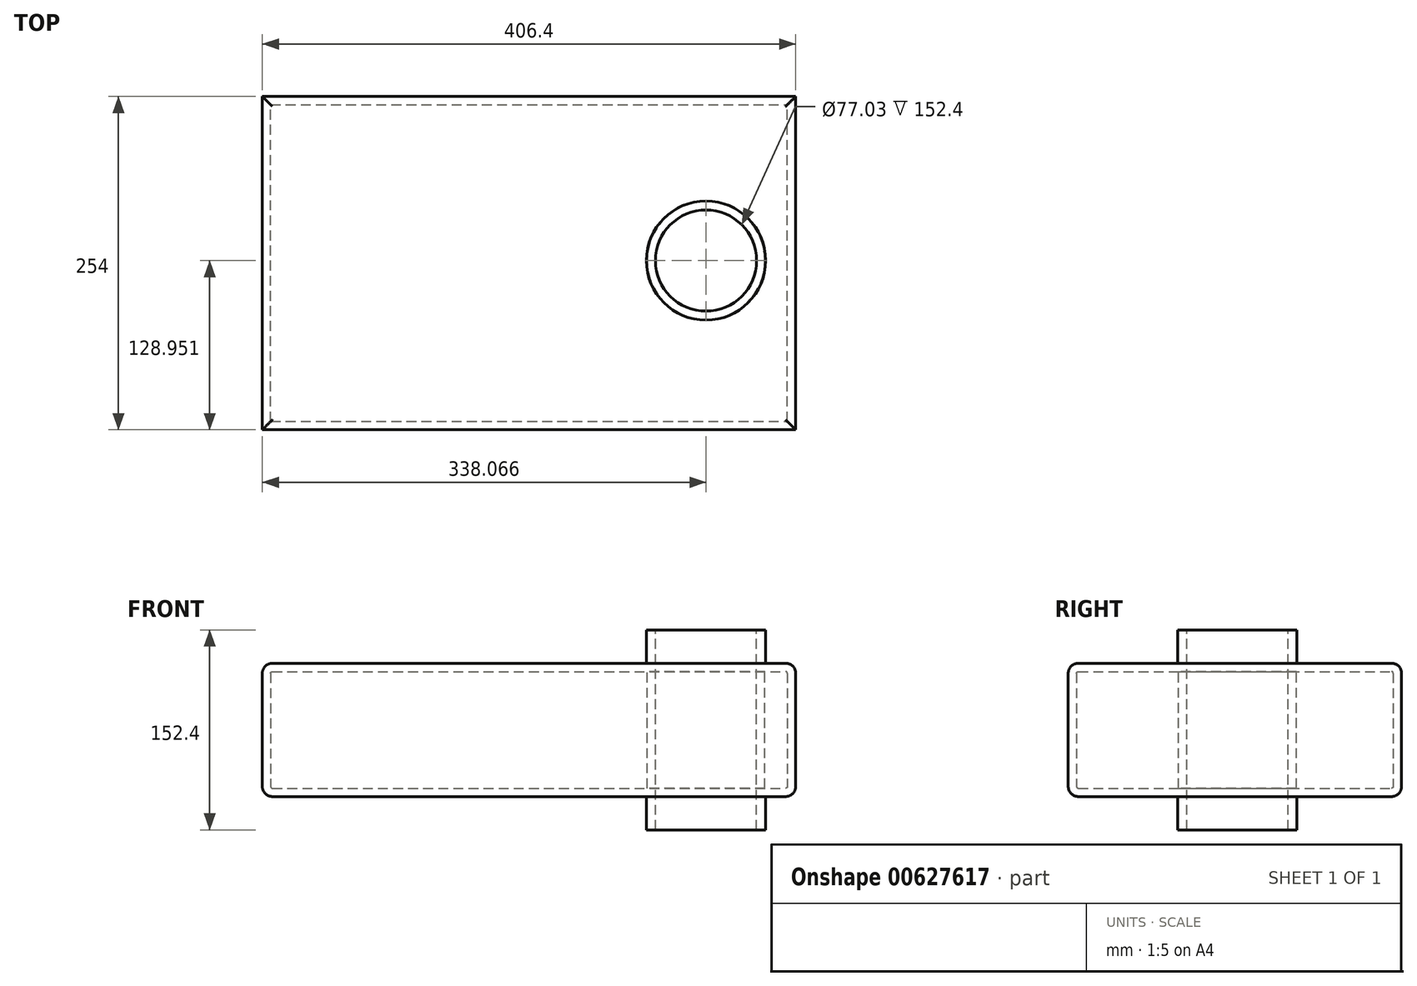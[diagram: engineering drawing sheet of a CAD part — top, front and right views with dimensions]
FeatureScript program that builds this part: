
annotation { "Feature Type Name" : "Feature", "Feature Type Description" : "" }
export const myFeature = defineFeature(function(context is Context, id is Id, definition is map)
    precondition{}
    {
        {
            var Q0;
            Q0=qCreatedBy(makeId("Top.planeOp"),FACE);
            var sketch = newSketch(context, id + "F0", { "sketchPlane" : qUnion([Q0])});
            skLineSegment(sketch, "E0.bottom", {"start": v(-406.4, 0) * mm, "end": v(0, 0) * mm});
            skLineSegment(sketch, "E0.top", {"start": v(-406.4, 254) * mm, "end": v(0, 254) * mm});
            skLineSegment(sketch, "E0.left", {"start": v(-406.4, 0) * mm, "end": v(-406.4, 254) * mm});
            skLineSegment(sketch, "E0.right", {"start": v(0, 0) * mm, "end": v(0, 254) * mm});
            skSolve(sketch);
        }
        {
            var Q0;
            Q0 = qSketchRegion(id + "F0", true);
            extrude(context, id + "F1", {"entities" : qUnion([Q0]), "depth" : 50.8 * mm, "offsetDistance" : 25.4 * mm});
        }
        {
            var Q0;
            Q0=makeQuery(id+"F1.opExtrude","CAP_EDGE",EDGE,{"disambiguationData":[OSD([sQuery(id+"F0.wireOp",EDGE,"E0.left")])],"isStart":false});
            var Q1;
            Q1=makeQuery(id+"F1.opExtrude","CAP_EDGE",EDGE,{"disambiguationData":[OSD([sQuery(id+"F0.wireOp",EDGE,"E0.bottom")])],"isStart":false});
            var Q2;
            Q2=makeQuery(id+"F1.opExtrude","CAP_EDGE",EDGE,{"disambiguationData":[OSD([sQuery(id+"F0.wireOp",EDGE,"E0.right")])],"isStart":false});
            var Q3;
            Q3=makeQuery(id+"F1.opExtrude","CAP_EDGE",EDGE,{"disambiguationData":[OSD([sQuery(id+"F0.wireOp",EDGE,"E0.top")])],"isStart":false});
            fillet(context, id + "F2", {"entities" : qUnion([Q0, Q1, Q2, Q3]), "radius" : 7.62 * mm, "tangentPropagation" : true, "allowEdgeOverflow" : false});
        }
        {
            var Q0;
            Q0=makeQuery(id+"F1.opExtrude","CAP_FACE",FACE,{"disambiguationData":[OSD([sQuery(id+"F0.wireOp",EDGE,"E0.bottom"),sQuery(id+"F0.wireOp",EDGE,"E0.top"),sQuery(id+"F0.wireOp",EDGE,"E0.left"),sQuery(id+"F0.wireOp",EDGE,"E0.right")])],"isStart":false});
            var sketch = newSketch(context, id + "F3", { "sketchPlane" : qUnion([Q0])});
            skCircle(sketch, "E1", {"center": v(-68.33, 128.95) * mm, "radius": 38.51 * mm});
            skSolve(sketch);
        }
        {
            var Q0;
            Q0=makeQuery(id+"F3.imprint","IMPRINT",FACE,{"disambiguationData":[TD([[makeQuery(id+"F3.imprint","IMPRINT",EDGE,{"derivedFrom":sQuery(id+"F3.wireOp",EDGE,"E1")}),1.0]])]});
            extrude(context, id + "F4", {"entities" : qUnion([Q0]), "operationType" : NewBodyOperationType.REMOVE, "endBound" : BoundingType.THROUGH_ALL, "oppositeDirection" : true, "depth" : 25.4 * mm, "offsetDistance" : 25.4 * mm});
        }
        {
            var Q0;
            Q0=makeQuery(id+"F1.opExtrude","CAP_FACE",FACE,{"disambiguationData":[OSD([sQuery(id+"F0.wireOp",EDGE,"E0.bottom"),sQuery(id+"F0.wireOp",EDGE,"E0.top"),sQuery(id+"F0.wireOp",EDGE,"E0.left"),sQuery(id+"F0.wireOp",EDGE,"E0.right")])],"isStart":true});
            shell(context, id + "F5", {"entities" : qUnion([Q0]), "thickness" : 6.35 * mm});
        }
        {
            var Q0;
            Q0=makeQuery(id+"F1.opExtrude","CAP_FACE",FACE,{"disambiguationData":[OSD([sQuery(id+"F0.wireOp",EDGE,"E0.bottom"),sQuery(id+"F0.wireOp",EDGE,"E0.top"),sQuery(id+"F0.wireOp",EDGE,"E0.left"),sQuery(id+"F0.wireOp",EDGE,"E0.right")])],"isStart":false});
            var sketch = newSketch(context, id + "F6", { "sketchPlane" : qUnion([Q0])});
            skCircle(sketch, "E2", {"center": v(-68.33, 128.95) * mm, "radius": 45.4 * mm});
            skSolve(sketch);
        }
        {
            var Q0;
            Q0=makeQuery(id+"F6.imprint","IMPRINT",FACE,{"disambiguationData":[TD([[makeQuery(id+"F6.imprint","IMPRINT",EDGE,{"derivedFrom":sQuery(id+"F6.wireOp",EDGE,"E2")}),1.0]])]});
            extrude(context, id + "F7", {"entities" : qUnion([Q0]), "operationType" : NewBodyOperationType.ADD, "depth" : 25.4 * mm, "offsetDistance" : 25.4 * mm});
        }
        {
            var Q0;
            Q0=makeQuery(id+"F1.opExtrude","SWEPT_BODY",BODY,{"disambiguationData":[OSD([sQuery(id+"F0.wireOp",EDGE,"E0.bottom"),sQuery(id+"F0.wireOp",EDGE,"E0.top"),sQuery(id+"F0.wireOp",EDGE,"E0.left"),sQuery(id+"F0.wireOp",EDGE,"E0.right")])]});
            var Q1;
            Q1=qCreatedBy(makeId("Top.planeOp"),FACE);
            mirror(context, id + "F8", {"operationType" : NewBodyOperationType.ADD, "entities" : qUnion([Q0]), "mirrorPlane" : qUnion([Q1])});
        }
    });
